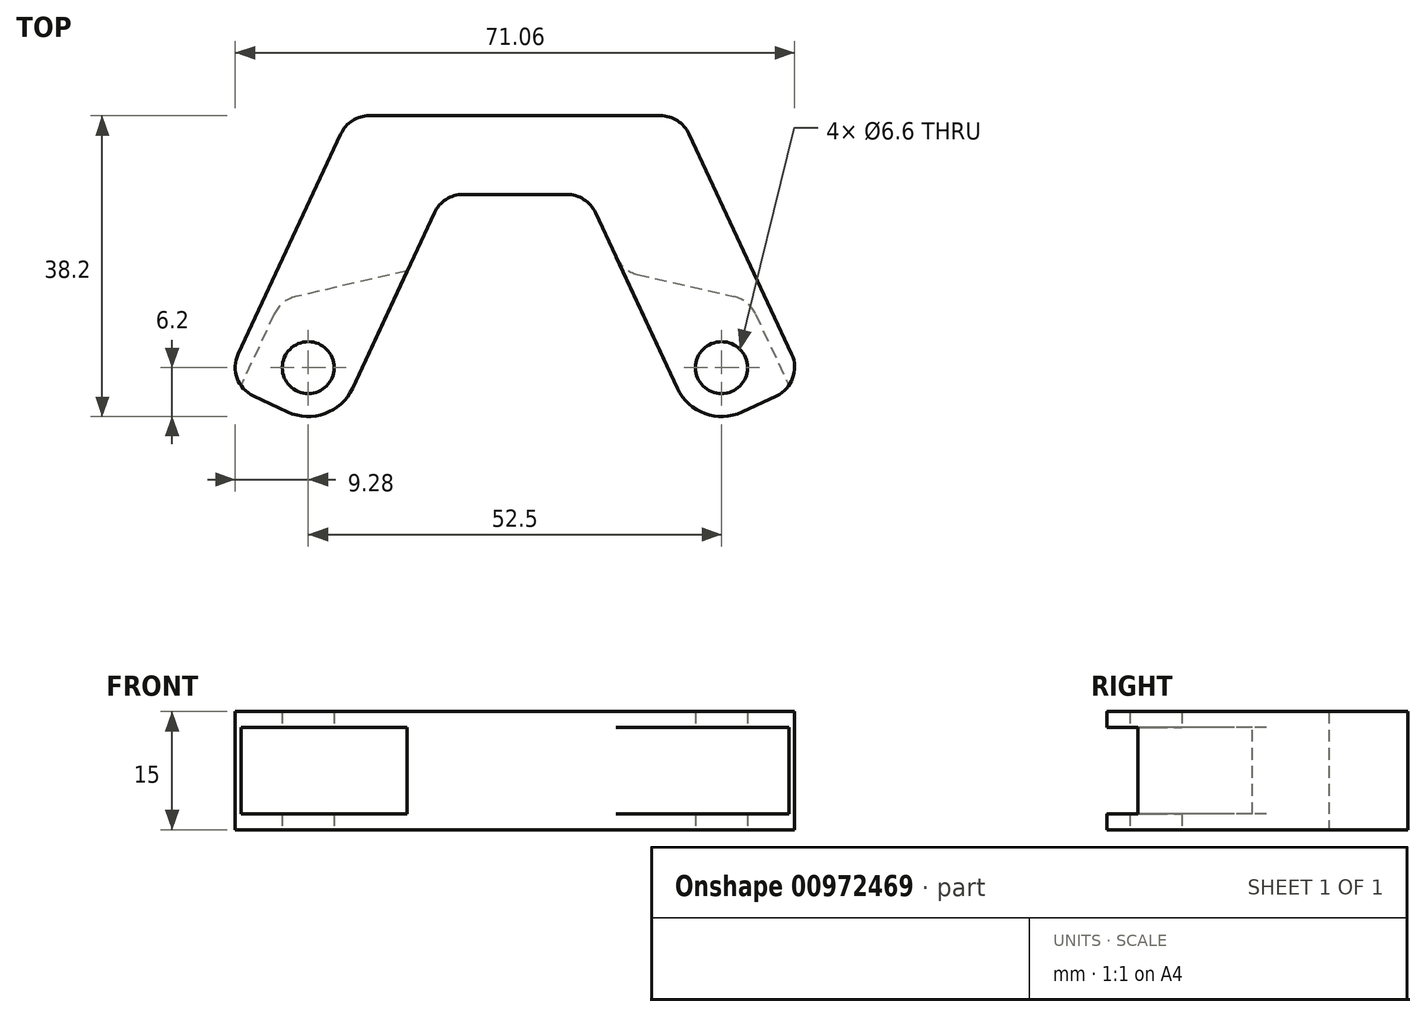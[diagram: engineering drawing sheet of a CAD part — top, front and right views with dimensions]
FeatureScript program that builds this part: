
annotation { "Feature Type Name" : "Feature", "Feature Type Description" : "" }
export const myFeature = defineFeature(function(context is Context, id is Id, definition is map)
    precondition{}
    {
        {
            var Q0;
            Q0=qCreatedBy(makeId("Top.planeOp"),FACE);
            var sketch = newSketch(context, id + "F0", { "sketchPlane" : qUnion([Q0])});
            skCircle(sketch, "E0", {"center": v(26.25, 0) * mm, "radius": 3.3 * mm});
            skCircle(sketch, "E1.MirrorC", {"center": v(-26.25, 0) * mm, "radius": 3.3 * mm});
            skSolve(sketch);
        }
        {
            var Q0;
            Q0=qCreatedBy(makeId("Top.planeOp"),FACE);
            var sketch = newSketch(context, id + "F1", { "sketchPlane" : qUnion([Q0])});
            skLineSegment(sketch, "E2", {"start": v(0, 22) * mm, "end": v(9.15, 22) * mm});
            skLineSegment(sketch, "E3", {"start": v(9.15, 22) * mm, "end": v(20.63, -2.62) * mm});
            skLineSegment(sketch, "E4", {"start": v(32.58, 7.25) * mm, "end": v(21.04, 32) * mm});
            skLineSegment(sketch, "E5", {"start": v(21.04, 32) * mm, "end": v(0, 32) * mm});
            skPoint(sketch, "E6.0", {"position": v(26.25, 0) * mm});
            skPoint(sketch, "E7", {"position": v(26, 0) * mm});
            skLineSegment(sketch, "E8", {"start": v(32.58, 7.25) * mm, "end": v(36.85, -1.9) * mm});
            skCircle(sketch, "E9.0", {"center": v(26.25, 0) * mm, "radius": 3.3 * mm});
            skCircle(sketch, "E10.0.0", {"center": v(26.25, 0) * mm, "radius": 3.3 * mm, "construction": true});
            skArc(sketch, "E11", {"start": v(20.63, -2.62) * mm, "mid": v(24.13, -5.83) * mm, "end": v(28.87, -5.62) * mm});
            skLineSegment(sketch, "E12", {"start": v(36.85, -1.9) * mm, "end": v(28.87, -5.62) * mm});
            skPoint(sketch, "E13.MirrorP", {"position": v(-26.25, 0) * mm});
            skCircle(sketch, "E14.MirrorC", {"center": v(-26.25, 0) * mm, "radius": 3.3 * mm});
            skPoint(sketch, "E15.MirrorP", {"position": v(-26, 0) * mm});
            skLineSegment(sketch, "E16.MirrorCS", {"start": v(-36.85, -1.9) * mm, "end": v(-28.87, -5.62) * mm});
            skCircle(sketch, "E17.MirrorC", {"center": v(-26.25, 0) * mm, "radius": 3.3 * mm, "construction": true});
            skLineSegment(sketch, "E18.MirrorCS", {"start": v(0, 22) * mm, "end": v(-9.15, 22) * mm});
            skArc(sketch, "E19.MirrorCS", {"start": v(-20.63, -2.62) * mm, "mid": v(-24.13, -5.83) * mm, "end": v(-28.87, -5.62) * mm});
            skLineSegment(sketch, "E20.MirrorCS", {"start": v(-32.58, 7.25) * mm, "end": v(-21.04, 32) * mm});
            skLineSegment(sketch, "E21.MirrorCS", {"start": v(-9.15, 22) * mm, "end": v(-20.63, -2.62) * mm});
            skLineSegment(sketch, "E22.MirrorCS", {"start": v(-32.58, 7.25) * mm, "end": v(-36.85, -1.9) * mm});
            skLineSegment(sketch, "E23.MirrorCS", {"start": v(-21.04, 32) * mm, "end": v(0, 32) * mm});
            skSolve(sketch);
        }
        {
            var Q0;
            Q0 = qSketchRegion(id + "F1", true);
            extrude(context, id + "F2", {"entities" : qUnion([Q0]), "endBound" : BoundingType.SYMMETRIC, "depth" : 15 * mm, "offsetDistance" : 25 * mm});
        }
        {
            var Q0;
            Q0 = qSketchRegion(id + "F0", true);
            extrude(context, id + "F3", {"entities" : qUnion([Q0]), "operationType" : NewBodyOperationType.REMOVE, "endBound" : BoundingType.THROUGH_ALL, "depth" : 25 * mm, "offsetDistance" : 25 * mm});
        }
        {
            var Q0;
            Q0=qCreatedBy(makeId("Top.planeOp"),FACE);
            var sketch = newSketch(context, id + "F4", { "sketchPlane" : qUnion([Q0])});
            skLineSegment(sketch, "E24.0", {"start": v(21.04, 32) * mm, "end": v(36.85, -1.9) * mm, "construction": true});
            skLineSegment(sketch, "E25", {"start": v(29.75, 8.58) * mm, "end": v(38.16, -9.46) * mm});
            skLineSegment(sketch, "E26", {"start": v(38.16, -9.46) * mm, "end": v(24.04, -14.28) * mm});
            skLineSegment(sketch, "E27", {"start": v(24.04, -14.28) * mm, "end": v(11.4, 12.82) * mm});
            skLineSegment(sketch, "E28", {"start": v(11.4, 12.82) * mm, "end": v(29.75, 8.58) * mm});
            skLineSegment(sketch, "E29.MirrorCS", {"start": v(-38.16, -9.46) * mm, "end": v(-24.04, -14.28) * mm});
            skLineSegment(sketch, "E30.MirrorCS", {"start": v(-24.04, -14.28) * mm, "end": v(-11.4, 12.82) * mm});
            skLineSegment(sketch, "E31.MirrorCS", {"start": v(-29.75, 8.58) * mm, "end": v(-38.16, -9.46) * mm});
            skLineSegment(sketch, "E32.MirrorCS", {"start": v(-11.4, 12.82) * mm, "end": v(-29.75, 8.58) * mm});
            skPoint(sketch, "E33.0", {"position": v(26.25, 0) * mm});
            skSolve(sketch);
        }
        {
            var Q0;
            Q0 = qSketchRegion(id + "F4", true);
            extrude(context, id + "F5", {"entities" : qUnion([Q0]), "operationType" : NewBodyOperationType.REMOVE, "endBound" : BoundingType.SYMMETRIC, "oppositeDirection" : true, "depth" : 11 * mm, "offsetDistance" : 25 * mm});
        }
        {
            var Q0;
            Q0=makeQuery(id+"F2.opExtrude","SWEPT_EDGE",EDGE,{"disambiguationData":[OSD([sQuery(id+"F1.wireOp",EDGE,"E2"),sQuery(id+"F1.wireOp",EDGE,"E3")])]});
            var Q1;
            Q1=makeQuery(id+"F2.opExtrude","SWEPT_EDGE",EDGE,{"disambiguationData":[OSD([sQuery(id+"F1.wireOp",EDGE,"3c0d8575-7c75-44c2-b176-444a6d5a51187.MirrorCS"),sQuery(id+"F1.wireOp",EDGE,"3c0d8575-7c75-44c2-b176-444a6d5a511811.MirrorCS")])]});
            var Q2;
            Q2=makeQuery(id+"F5.boolean.opBoolean","COPY",EDGE,{"derivedFrom":makeQuery(id+"F5.opExtrude","SWEPT_EDGE",EDGE,{"disambiguationData":[OSD([sQuery(id+"F4.wireOp",EDGE,"E25"),sQuery(id+"F4.wireOp",EDGE,"E28")])]})});
            var Q3;
            Q3=makeQuery(id+"F5.boolean.opBoolean","COPY",EDGE,{"derivedFrom":makeQuery(id+"F5.opExtrude","SWEPT_EDGE",EDGE,{"disambiguationData":[OSD([sQuery(id+"F4.wireOp",EDGE,"E31.MirrorCS"),sQuery(id+"F4.wireOp",EDGE,"E32.MirrorCS")])]})});
            var Q4;
            Q4=makeQuery(id+"F5.boolean.opBoolean","INTERSECT",EDGE,{"derivedFrom":[makeQuery(id+"F2.opExtrude","SWEPT_FACE",FACE,{"disambiguationData":[OSD([sQuery(id+"F1.wireOp",EDGE,"3c0d8575-7c75-44c2-b176-444a6d5a51180.MirrorCS"),sQuery(id+"F1.wireOp",EDGE,"3c0d8575-7c75-44c2-b176-444a6d5a51187.MirrorCS")])]}),makeQuery(id+"F5.opExtrude","SWEPT_FACE",FACE,{"disambiguationData":[OSD([sQuery(id+"F4.wireOp",EDGE,"E32.MirrorCS")])]})]});
            var Q5;
            Q5=makeQuery(id+"F5.boolean.opBoolean","INTERSECT",EDGE,{"derivedFrom":[makeQuery(id+"F2.opExtrude","SWEPT_FACE",FACE,{"disambiguationData":[OSD([sQuery(id+"F1.wireOp",EDGE,"E3"),sQuery(id+"F1.wireOp",EDGE,"Zfp1O7tn-kqPr-JE8E-h24D-LB3VAzdz07G7")])]}),makeQuery(id+"F5.opExtrude","SWEPT_FACE",FACE,{"disambiguationData":[OSD([sQuery(id+"F4.wireOp",EDGE,"E28")])]})]});
            var Q6;
            Q6=makeQuery(id+"F2.opExtrude","SWEPT_EDGE",EDGE,{"disambiguationData":[OSD([sQuery(id+"F1.wireOp",EDGE,"E8"),sQuery(id+"F1.wireOp",EDGE,"cd8894c0-da2c-4d53-99b0-34fd4b2b3cc5")])]});
            var Q7;
            Q7=makeQuery(id+"F2.opExtrude","SWEPT_EDGE",EDGE,{"disambiguationData":[OSD([sQuery(id+"F1.wireOp",EDGE,"3c0d8575-7c75-44c2-b176-444a6d5a51182.MirrorCS"),sQuery(id+"F1.wireOp",EDGE,"3c0d8575-7c75-44c2-b176-444a6d5a51188.MirrorCS")])]});
            var Q8;
            Q8=makeQuery(id+"F2.opExtrude","SWEPT_EDGE",EDGE,{"disambiguationData":[OSD([sQuery(id+"F1.wireOp",EDGE,"3c0d8575-7c75-44c2-b176-444a6d5a51185.MirrorCS"),sQuery(id+"F1.wireOp",EDGE,"3c0d8575-7c75-44c2-b176-444a6d5a51186.MirrorCS")])]});
            var Q9;
            Q9=makeQuery(id+"F2.opExtrude","SWEPT_EDGE",EDGE,{"disambiguationData":[OSD([sQuery(id+"F1.wireOp",EDGE,"E4"),sQuery(id+"F1.wireOp",EDGE,"E5")])]});
            var Q10;
            {var subQ0=sQuery(id+"F1.wireOp",EDGE,"cd8894c0-da2c-4d53-99b0-34fd4b2b3cc5");var subQ1=sQuery(id+"F1.wireOp",EDGE,"Zfp1O7tn-kqPr-JE8E-h24D-LB3VAzdz07G7");Q10=makeQuery(id+"F5.boolean.opBoolean","SPLIT",EDGE,{"disambiguationData":[TD([makeQuery(id+"F5.opExtrude","CAP_FACE",FACE,{"disambiguationData":[OSD([sQuery(id+"F4.wireOp",EDGE,"E25"),sQuery(id+"F4.wireOp",EDGE,"E26"),sQuery(id+"F4.wireOp",EDGE,"E27"),sQuery(id+"F4.wireOp",EDGE,"E28")])],"isStart":true})])],"derivedFrom":makeQuery(id+"F2.opExtrude","SWEPT_EDGE",EDGE,{"disambiguationData":[OSD([subQ1,subQ0])]})});}
            var Q11;
            {var subQ0=sQuery(id+"F1.wireOp",EDGE,"cd8894c0-da2c-4d53-99b0-34fd4b2b3cc5");var subQ1=sQuery(id+"F1.wireOp",EDGE,"Zfp1O7tn-kqPr-JE8E-h24D-LB3VAzdz07G7");Q11=makeQuery(id+"F5.boolean.opBoolean","SPLIT",EDGE,{"disambiguationData":[TD([makeQuery(id+"F5.opExtrude","CAP_FACE",FACE,{"disambiguationData":[OSD([sQuery(id+"F4.wireOp",EDGE,"E25"),sQuery(id+"F4.wireOp",EDGE,"E26"),sQuery(id+"F4.wireOp",EDGE,"E27"),sQuery(id+"F4.wireOp",EDGE,"E28")])],"isStart":false})])],"derivedFrom":makeQuery(id+"F2.opExtrude","SWEPT_EDGE",EDGE,{"disambiguationData":[OSD([subQ1,subQ0])]})});}
            var Q12;
            {var subQ0=sQuery(id+"F1.wireOp",EDGE,"3c0d8575-7c75-44c2-b176-444a6d5a51188.MirrorCS");var subQ2=sQuery(id+"F1.wireOp",EDGE,"3c0d8575-7c75-44c2-b176-444a6d5a51180.MirrorCS");Q12=makeQuery(id+"F5.boolean.opBoolean","SPLIT",EDGE,{"disambiguationData":[TD([makeQuery(id+"F5.opExtrude","CAP_FACE",FACE,{"disambiguationData":[OSD([sQuery(id+"F4.wireOp",EDGE,"E29.MirrorCS"),sQuery(id+"F4.wireOp",EDGE,"E30.MirrorCS"),sQuery(id+"F4.wireOp",EDGE,"E31.MirrorCS"),sQuery(id+"F4.wireOp",EDGE,"E32.MirrorCS")])],"isStart":true})])],"derivedFrom":makeQuery(id+"F2.opExtrude","SWEPT_EDGE",EDGE,{"disambiguationData":[OSD([subQ2,subQ0])]})});}
            var Q13;
            {var subQ0=sQuery(id+"F1.wireOp",EDGE,"3c0d8575-7c75-44c2-b176-444a6d5a51188.MirrorCS");var subQ2=sQuery(id+"F1.wireOp",EDGE,"3c0d8575-7c75-44c2-b176-444a6d5a51180.MirrorCS");Q13=makeQuery(id+"F5.boolean.opBoolean","SPLIT",EDGE,{"disambiguationData":[TD([makeQuery(id+"F5.opExtrude","CAP_FACE",FACE,{"disambiguationData":[OSD([sQuery(id+"F4.wireOp",EDGE,"E29.MirrorCS"),sQuery(id+"F4.wireOp",EDGE,"E30.MirrorCS"),sQuery(id+"F4.wireOp",EDGE,"E31.MirrorCS"),sQuery(id+"F4.wireOp",EDGE,"E32.MirrorCS")])],"isStart":false})])],"derivedFrom":makeQuery(id+"F2.opExtrude","SWEPT_EDGE",EDGE,{"disambiguationData":[OSD([subQ2,subQ0])]})});}
            var Q14;
            Q14=makeQuery(id+"F2.opExtrude","SWEPT_EDGE",EDGE,{"disambiguationData":[OSD([sQuery(id+"F1.wireOp",EDGE,"E18.MirrorCS"),sQuery(id+"F1.wireOp",EDGE,"E21.MirrorCS")])]});
            var Q15;
            Q15=makeQuery(id+"F2.opExtrude","SWEPT_EDGE",EDGE,{"disambiguationData":[OSD([sQuery(id+"F1.wireOp",EDGE,"E16.MirrorCS"),sQuery(id+"F1.wireOp",EDGE,"E22.MirrorCS")])]});
            var Q16;
            Q16=makeQuery(id+"F2.opExtrude","SWEPT_EDGE",EDGE,{"disambiguationData":[OSD([sQuery(id+"F1.wireOp",EDGE,"E20.MirrorCS"),sQuery(id+"F1.wireOp",EDGE,"E23.MirrorCS")])]});
            fillet(context, id + "F6", {"entities" : qUnion([Q0, Q1, Q2, Q3, Q4, Q5, Q6, Q7, Q8, Q9, Q10, Q11, Q12, Q13, Q14, Q15, Q16]), "radius" : 4 * mm, "tangentPropagation" : true, "allowEdgeOverflow" : false});
        }
    });
